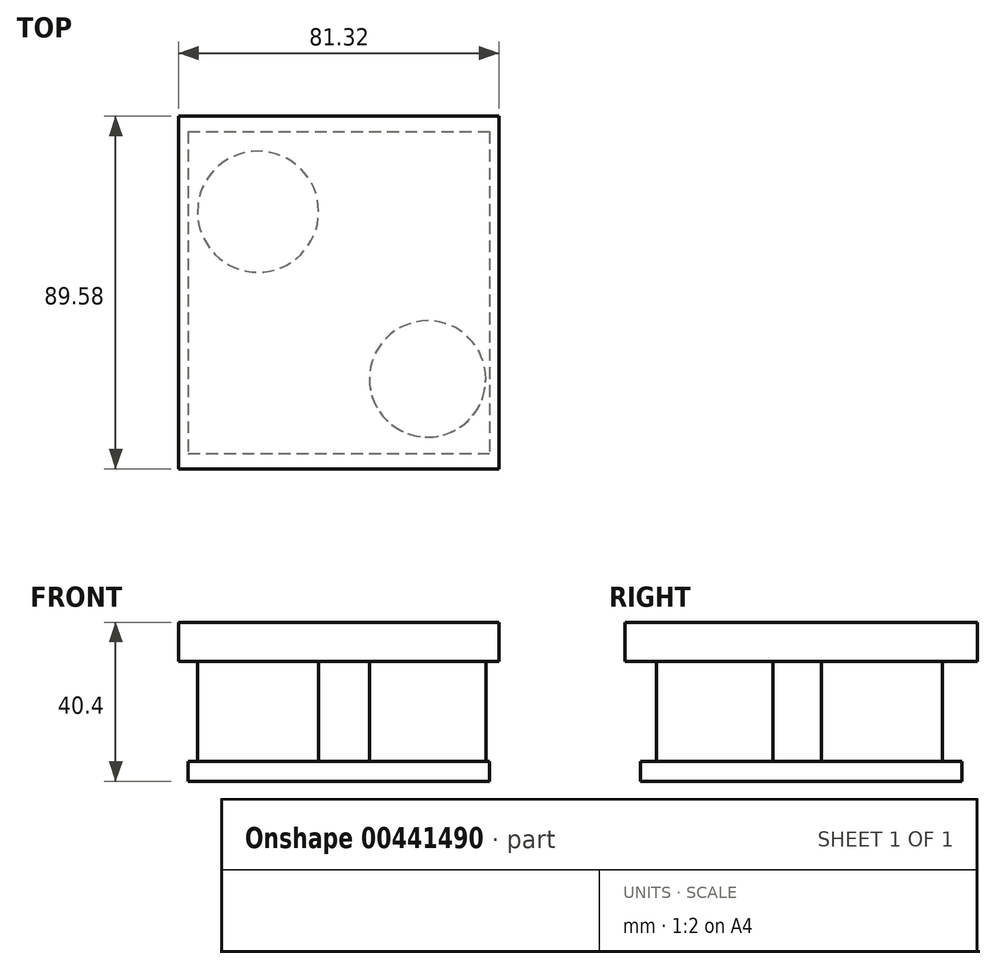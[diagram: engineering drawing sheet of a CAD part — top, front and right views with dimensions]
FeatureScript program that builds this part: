
annotation { "Feature Type Name" : "Feature", "Feature Type Description" : "" }
export const myFeature = defineFeature(function(context is Context, id is Id, definition is map)
    precondition{}
    {
        {
            var Q0;
            Q0=qCreatedBy(makeId("Top.planeOp"),FACE);
            var sketch = newSketch(context, id + "F0", { "sketchPlane" : qUnion([Q0])});
            skLineSegment(sketch, "E0.bottom", {"start": v(40.66, 44.79) * mm, "end": v(-40.66, 44.79) * mm});
            skLineSegment(sketch, "E0.top", {"start": v(40.66, -44.79) * mm, "end": v(-40.66, -44.79) * mm});
            skLineSegment(sketch, "E0.left", {"start": v(40.66, 44.79) * mm, "end": v(40.66, -44.79) * mm});
            skLineSegment(sketch, "E0.right", {"start": v(-40.66, 44.79) * mm, "end": v(-40.66, -44.79) * mm});
            skPoint(sketch, "E0.middle", {"position": v(0, 0) * mm});
            skSolve(sketch);
        }
        {
            var Q0;
            Q0 = qSketchRegion(id + "F0", true);
            extrude(context, id + "F1", {"entities" : qUnion([Q0]), "depth" : 10 * mm});
        }
        {
            var Q0;
            Q0=makeQuery(id+"F1.opExtrude","CAP_FACE",FACE,{"disambiguationData":[OSD([sQuery(id+"F0.wireOp",EDGE,"E0.bottom"),sQuery(id+"F0.wireOp",EDGE,"E0.top"),sQuery(id+"F0.wireOp",EDGE,"E0.left"),sQuery(id+"F0.wireOp",EDGE,"E0.right")])],"isStart":true});
            var sketch = newSketch(context, id + "F2", { "sketchPlane" : qUnion([Q0])});
            skCircle(sketch, "E1", {"center": v(-20.52, -20.54) * mm, "radius": 15.38 * mm});
            skCircle(sketch, "E2", {"center": v(22.55, 21.97) * mm, "radius": 14.79 * mm});
            skSolve(sketch);
        }
        {
            var Q0;
            Q0 = qSketchRegion(id + "F2", true);
            var Q1;
            Q1=makeQuery(id+"F2.imprint","IMPRINT",FACE,{"disambiguationData":[TD([[makeQuery(id+"F2.imprint","IMPRINT",EDGE,{"derivedFrom":sQuery(id+"F2.wireOp",EDGE,"E2")}),1.0]])]});
            extrude(context, id + "F3", {"entities" : qUnion([Q0, Q1]), "operationType" : NewBodyOperationType.ADD, "depth" : 25.4 * mm});
        }
        {
            var Q0;
            Q0=makeQuery(id+"F3.opExtrude","CAP_FACE",FACE,{"disambiguationData":[OSD([sQuery(id+"F2.wireOp",EDGE,"E2")])],"isStart":false});
            var sketch = newSketch(context, id + "F4", { "sketchPlane" : qUnion([Q0])});
            skLineSegment(sketch, "E3.bottom", {"start": v(-38.3, -40.86) * mm, "end": v(38.3, -40.86) * mm});
            skLineSegment(sketch, "E3.top", {"start": v(-38.3, 40.86) * mm, "end": v(38.3, 40.86) * mm});
            skLineSegment(sketch, "E3.left", {"start": v(-38.3, -40.86) * mm, "end": v(-38.3, 40.86) * mm});
            skLineSegment(sketch, "E3.right", {"start": v(38.3, -40.86) * mm, "end": v(38.3, 40.86) * mm});
            skPoint(sketch, "E3.middle", {"position": v(0, 0) * mm});
            skSolve(sketch);
        }
        {
            var Q0;
            Q0 = qSketchRegion(id + "F4", true);
            extrude(context, id + "F5", {"entities" : qUnion([Q0]), "operationType" : NewBodyOperationType.ADD, "depth" : 5 * mm});
        }
    });
